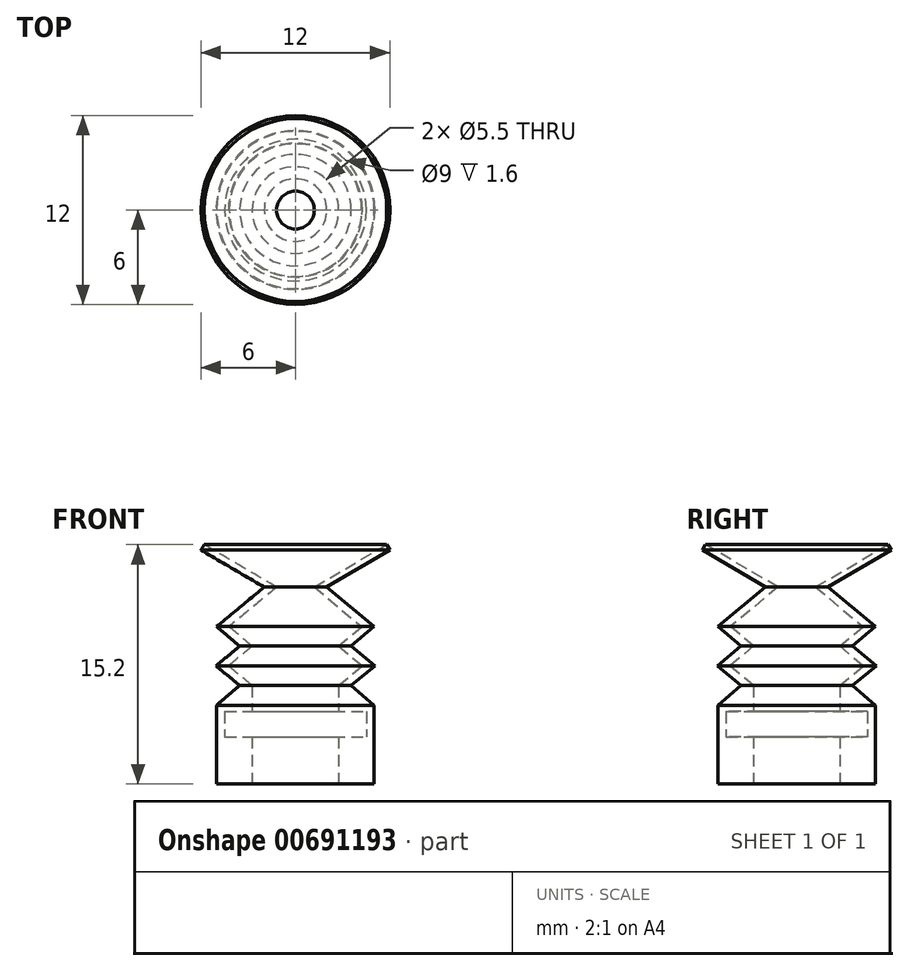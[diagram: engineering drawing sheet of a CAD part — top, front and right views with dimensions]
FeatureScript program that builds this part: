
annotation { "Feature Type Name" : "Feature", "Feature Type Description" : "" }
export const myFeature = defineFeature(function(context is Context, id is Id, definition is map)
    precondition{}
    {
        {
            var Q0;
            Q0=qCreatedBy(makeId("Front.planeOp"),FACE);
            var sketch = newSketch(context, id + "F0", { "sketchPlane" : qUnion([Q0])});
            skLineSegment(sketch, "E0", {"start": v(2.75, 0) * mm, "end": v(2.75, 3) * mm});
            skLineSegment(sketch, "E1", {"start": v(2.75, 3) * mm, "end": v(4.5, 3) * mm});
            skLineSegment(sketch, "E2", {"start": v(4.5, 3) * mm, "end": v(4.5, 4.6) * mm});
            skLineSegment(sketch, "E3", {"start": v(4.5, 4.6) * mm, "end": v(2.75, 4.6) * mm});
            skLineSegment(sketch, "E4", {"start": v(4.26, 7.5) * mm, "end": v(2.75, 8.75) * mm});
            skLineSegment(sketch, "E5", {"start": v(2.75, 8.75) * mm, "end": v(4.2, 10) * mm});
            skLineSegment(sketch, "E6", {"start": v(4.2, 10) * mm, "end": v(1.2, 12.5) * mm});
            skLineSegment(sketch, "E7", {"start": v(1.2, 12.5) * mm, "end": v(5.8, 15.2) * mm});
            skLineSegment(sketch, "E8", {"start": v(5.8, 15.2) * mm, "end": v(6, 14.86) * mm});
            skLineSegment(sketch, "E9", {"start": v(6, 14.86) * mm, "end": v(1.99, 12.5) * mm});
            skLineSegment(sketch, "E10", {"start": v(1.99, 12.5) * mm, "end": v(5, 10) * mm});
            skLineSegment(sketch, "E11", {"start": v(5, 10) * mm, "end": v(3.54, 8.75) * mm});
            skLineSegment(sketch, "E12", {"start": v(3.54, 8.75) * mm, "end": v(5.05, 7.5) * mm});
            skLineSegment(sketch, "E13", {"start": v(5.05, 7.5) * mm, "end": v(3.54, 6.25) * mm});
            skLineSegment(sketch, "E14", {"start": v(3.54, 6.25) * mm, "end": v(5, 5) * mm});
            skLineSegment(sketch, "E15", {"start": v(5, 5) * mm, "end": v(5, 0) * mm});
            skLineSegment(sketch, "E16", {"start": v(5, 0) * mm, "end": v(2.75, 0) * mm});
            skLineSegment(sketch, "E17", {"start": v(0, 0) * mm, "end": v(0, 9.35) * mm, "construction": true});
            skLineSegment(sketch, "E18", {"start": v(4.26, 7.5) * mm, "end": v(2.75, 6.25) * mm});
            skLineSegment(sketch, "E19", {"start": v(2.75, 4.6) * mm, "end": v(2.75, 6.25) * mm});
            skSolve(sketch);
        }
        {
            var Q0;
            Q0=makeQuery(id+"F0.imprint","IMPRINT",FACE,{"disambiguationData":[TD([[makeQuery(id+"F0.imprint","IMPRINT",EDGE,{"derivedFrom":sQuery(id+"F0.wireOp",EDGE,"E0")}),-1.0]])]});
            var Q1;
            Q1=sQuery(id+"F0.wireOp",EDGE,"E17");
            revolve(context, id + "F1", {"entities" : qUnion([Q0]), "axis" : qUnion([Q1]), "revolveType" : RevolveType.FULL});
        }
    });
